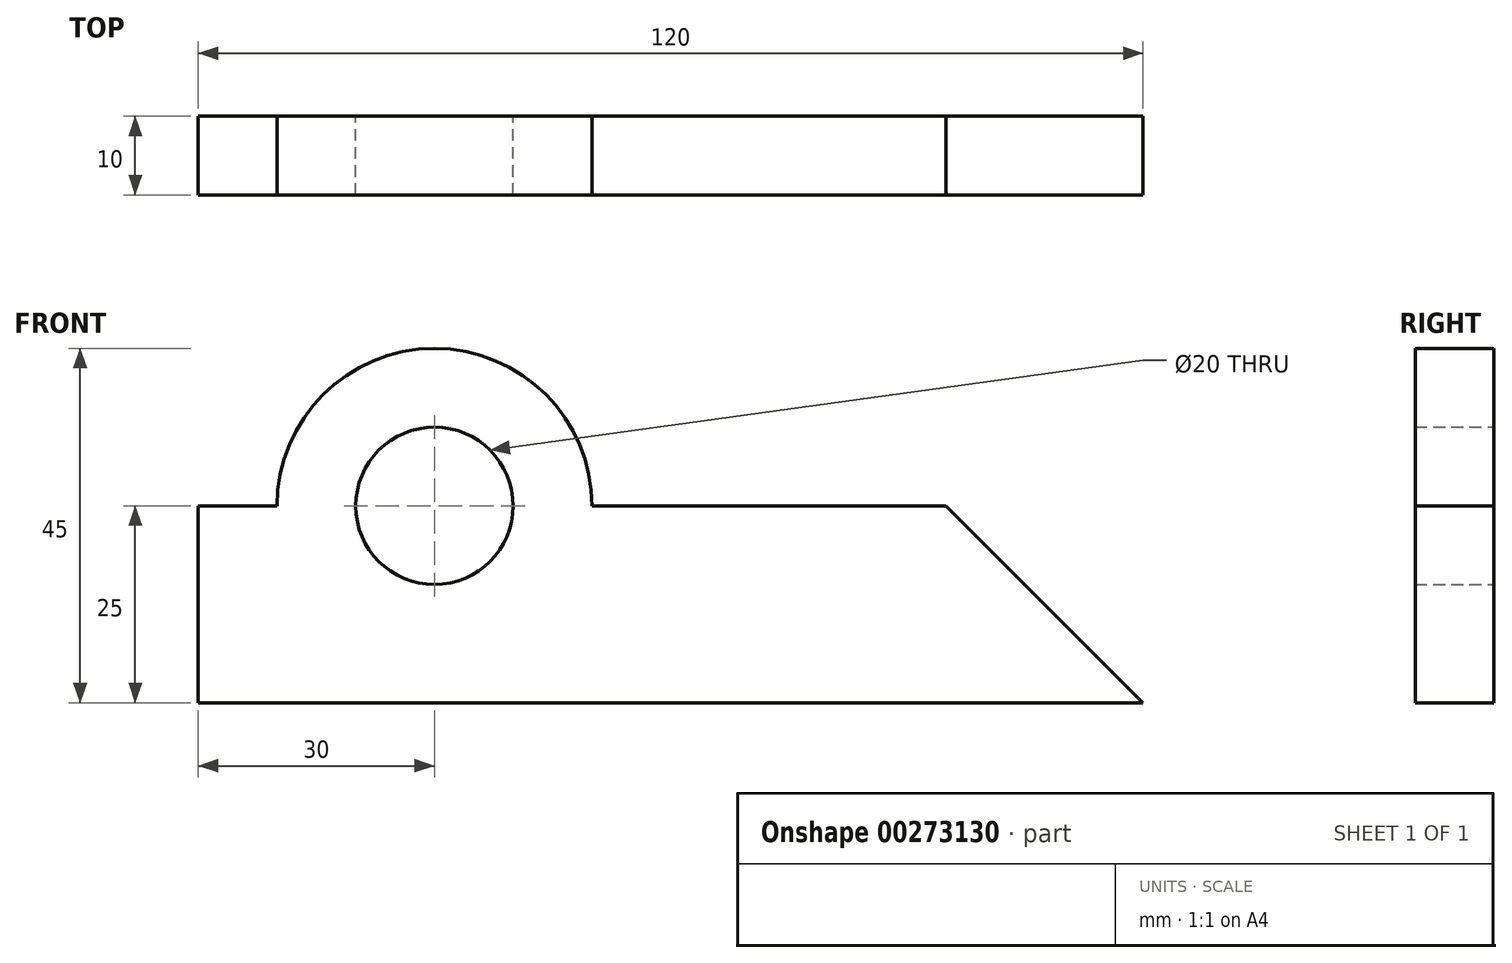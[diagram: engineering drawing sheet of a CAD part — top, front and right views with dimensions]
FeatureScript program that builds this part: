
annotation { "Feature Type Name" : "Feature", "Feature Type Description" : "" }
export const myFeature = defineFeature(function(context is Context, id is Id, definition is map)
    precondition{}
    {
        {
            var Q0;
            Q0=qCreatedBy(makeId("Front.planeOp"),FACE);
            var sketch = newSketch(context, id + "F0", { "sketchPlane" : qUnion([Q0])});
            skLineSegment(sketch, "E0", {"start": v(0, 0) * mm, "end": v(0, 25) * mm});
            skLineSegment(sketch, "E1", {"start": v(0, 0) * mm, "end": v(120, 0) * mm});
            skLineSegment(sketch, "E2", {"start": v(120, 0) * mm, "end": v(95, 25) * mm});
            skCircle(sketch, "E3", {"center": v(30, 25) * mm, "radius": 10 * mm});
            skArc(sketch, "E4", {"start": v(10, 25) * mm, "mid": v(30, 45) * mm, "end": v(50, 25) * mm});
            skLineSegment(sketch, "E5", {"start": v(0, 25) * mm, "end": v(10, 25) * mm});
            skLineSegment(sketch, "E6", {"start": v(50, 25) * mm, "end": v(95, 25) * mm});
            skSolve(sketch);
        }
        {
            var Q0;
            Q0=makeQuery(id+"F0.imprint","IMPRINT",FACE,{"disambiguationData":[TD([[makeQuery(id+"F0.imprint","IMPRINT",EDGE,{"derivedFrom":sQuery(id+"F0.wireOp",EDGE,"E0")}),-1.0]])]});
            extrude(context, id + "F1", {"entities" : qUnion([Q0]), "depth" : 10 * mm});
        }
    });
